# Revit family: HeatPump_AirToWater_Rheem_15kW_Vertical_LowGWP
name_source: partatom
category: Mechanical Equipment
units: mm (PartAtom-declared; Revit-internal decimal feet)

## family parameters
Always vertical = Yes
Classification = None
Cut with Voids When Loaded = No
OmniClass Number = 23.33.17.00
OmniClass Title = Heat Pumps
Part Type = Normal
Room Calculation Point = No
Round Connector Dimension = Use Diameter
Shared = No
Work Plane-Based = No

## types (2) — shared parameters
ApparentLoad = 15 VA
Assembly Code = D3020
BodyMaterial = Aluminium_PowderCoat_Rheem_White
FanHeight = 90 mm  [stored 0.295276 ft]
FanMaterial = Metal_Vent_Rheem_HeatPump_AirSource
IfcExportAs = IfcPump
IfcExportType = USERDEFINED
Manufacturer = Rheem
ManufacturerOverallDepth = 565 mm  [stored 1.85367 ft]
ManufacturerOverallHeight = 1074 mm  [stored 3.52362 ft]
ManufacturerOverallWidth = 1250 mm  [stored 4.10105 ft]
ManufacturerURLProductSpecific = https://www.rheem.com.au
ModifiedIssue = 20240801 $
PowerFactor = 1
ScreenMaterial = Metal_Vent_Rheem_HeatPump_Wire
URL = https://www.rheem.com.au
Uniclass2015Code = Pr_70_60_37_04
Uniclass2015Title = Air to water heat pumps
Uniclass2015Version = v1.33
Voltage = 230 V
zero-valued in all types: Default Elevation

## per-type parameters (varying)
| type | Description | FanFrame | ManufacturerSpecCode | Model | Type Comments |
| Ducted (95201500) | Rheem’s YF Series Commercial heat pump uses 1234yf refrigerant which has an ultra-low Global Warming Potential (GWP) of <1. Delivering hot water up to 65°C and operating in ambient temperatures to a low of 0°C with an improved Coefficient of Performance (COP) of up to 4.23 at 20°C ambient. Ducted models are designed with high static fans to enable reject air to be convey from the room. Models are  available in vertical and stackable horizontal discharge options. | Yes | 95201500 | 95201500 | HeatPump - AirToWater - 15kW - Vertical - LowGWP - Ducted |
| Non Ducted (95301500) | Rheem’s YF Series Commercial heat pump uses 1234yf refrigerant which has an ultra-low Global Warming Potential (GWP) of <1. Delivering hot water up to 65°C and operating in ambient temperatures to a low of 0°C with an improved Coefficient of Performance (COP) of up to 4.23 at 20°C ambient. Non ducted models are designed with electronically commutated fans for improved performance and are generally designed for outdoor installation, but may be installed indoors if a sufficient supply of heat energy is available. Models are  available in vertical and stackable horizontal discharge options. | No | 95301500 | 95301500 | HeatPump - AirToWater - 15kW - Vertical - LowGWP - Non Ducted |

note: [stored X ft] marks values corroborated as IEEE doubles in the binary element streams (Revit-internal decimal feet)

## geometry (parser evidence)
native form markers: Sweep x7
no freeform markers — native parametric forms only
